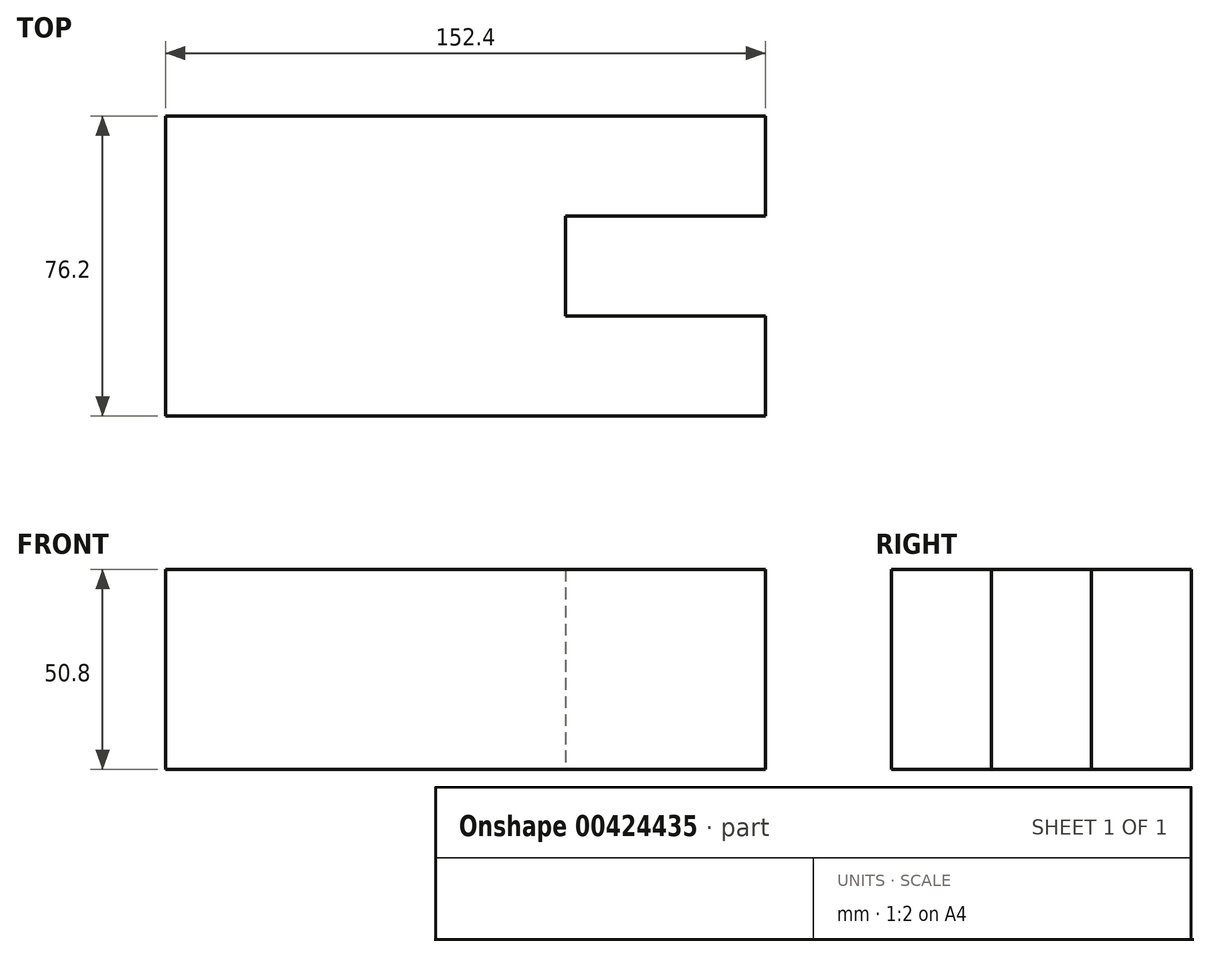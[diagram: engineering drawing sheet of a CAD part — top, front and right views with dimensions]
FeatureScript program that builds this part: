
annotation { "Feature Type Name" : "Feature", "Feature Type Description" : "" }
export const myFeature = defineFeature(function(context is Context, id is Id, definition is map)
    precondition{}
    {
        {
            var Q0;
            Q0=qCreatedBy(makeId("Top.planeOp"),FACE);
            var sketch = newSketch(context, id + "F0", { "sketchPlane" : qUnion([Q0])});
            skLineSegment(sketch, "E0", {"start": v(0, 0) * mm, "end": v(0, 76.2) * mm});
            skLineSegment(sketch, "E1", {"start": v(0, 76.2) * mm, "end": v(152.4, 76.2) * mm});
            skLineSegment(sketch, "E2", {"start": v(0, 0) * mm, "end": v(152.4, 0) * mm});
            skLineSegment(sketch, "E3", {"start": v(152.4, 76.2) * mm, "end": v(152.4, 50.8) * mm});
            skLineSegment(sketch, "E4", {"start": v(152.4, 50.8) * mm, "end": v(101.6, 50.8) * mm});
            skLineSegment(sketch, "E5", {"start": v(101.6, 50.8) * mm, "end": v(101.6, 25.4) * mm});
            skLineSegment(sketch, "E6", {"start": v(101.6, 25.4) * mm, "end": v(152.4, 25.4) * mm});
            skLineSegment(sketch, "E7", {"start": v(152.4, 25.4) * mm, "end": v(152.4, 0) * mm});
            skSolve(sketch);
        }
        {
            var Q0;
            Q0 = qSketchRegion(id + "F0", true);
            extrude(context, id + "F1", {"entities" : qUnion([Q0]), "depth" : 50.8 * mm});
        }
    });
